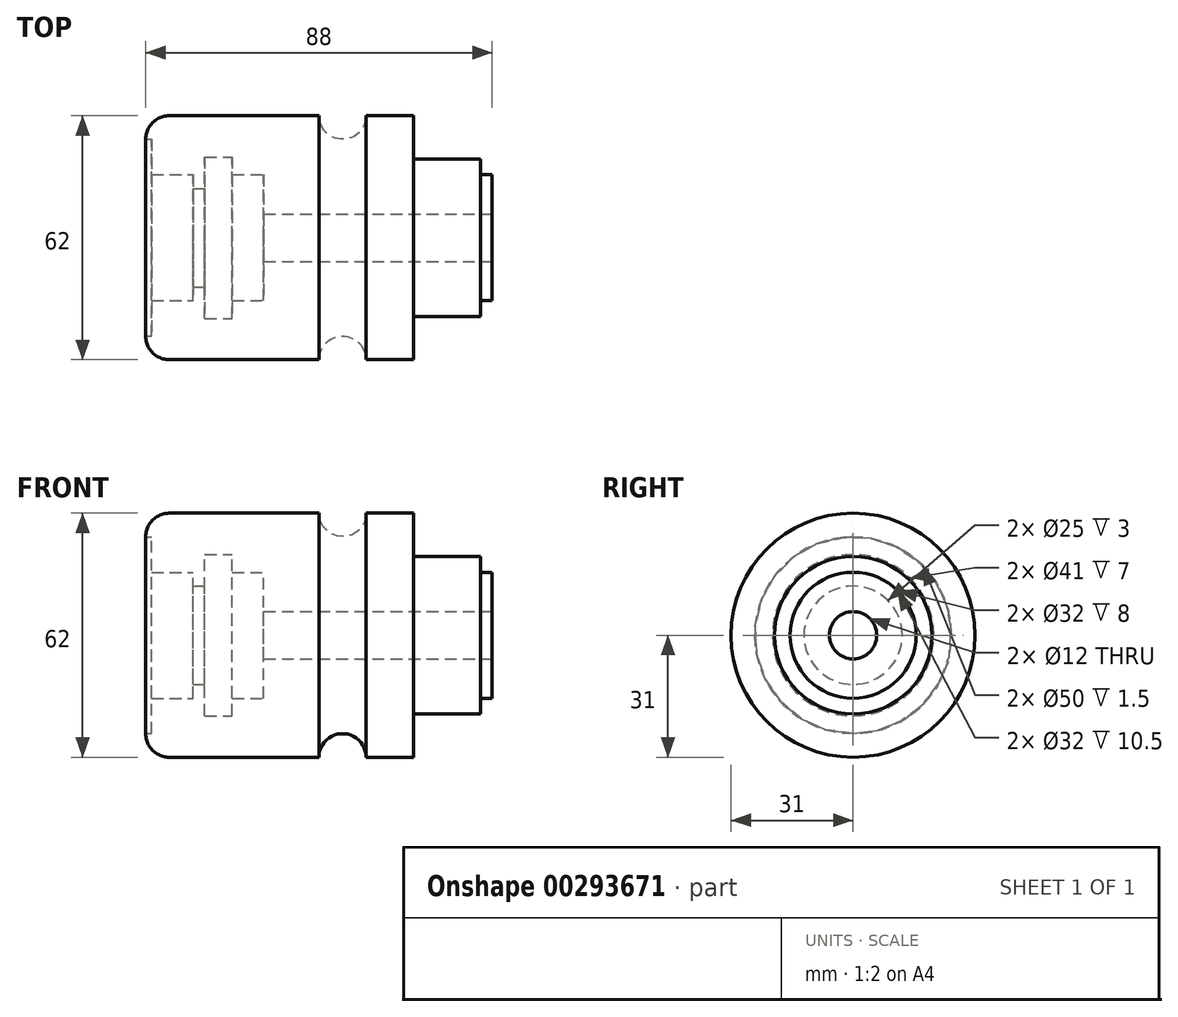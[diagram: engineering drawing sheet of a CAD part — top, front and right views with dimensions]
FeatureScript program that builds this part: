
annotation { "Feature Type Name" : "Feature", "Feature Type Description" : "" }
export const myFeature = defineFeature(function(context is Context, id is Id, definition is map)
    precondition{}
    {
        {
            var Q0;
            Q0=qCreatedBy(makeId("Front.planeOp"),FACE);
            var sketch = newSketch(context, id + "F0", { "sketchPlane" : qUnion([Q0])});
            skLineSegment(sketch, "E0", {"start": v(0, 31) * mm, "end": v(68, 31) * mm});
            skLineSegment(sketch, "E1", {"start": v(68, 31) * mm, "end": v(68, 20) * mm});
            skLineSegment(sketch, "E2", {"start": v(68, 20) * mm, "end": v(85, 20) * mm});
            skLineSegment(sketch, "E3", {"start": v(85, 20) * mm, "end": v(85, 16) * mm});
            skLineSegment(sketch, "E4", {"start": v(85, 16) * mm, "end": v(88, 16) * mm});
            skLineSegment(sketch, "E5", {"start": v(88, 16) * mm, "end": v(88, 0) * mm});
            skLineSegment(sketch, "E6", {"start": v(0, 0) * mm, "end": v(0, 31) * mm});
            skLineSegment(sketch, "E7", {"start": v(0, 25) * mm, "end": v(1.5, 25) * mm});
            skLineSegment(sketch, "E8", {"start": v(1.5, 25) * mm, "end": v(1.5, 0) * mm});
            skLineSegment(sketch, "E9", {"start": v(1.5, 16) * mm, "end": v(12, 16) * mm});
            skLineSegment(sketch, "E10", {"start": v(12, 16) * mm, "end": v(12, 0) * mm});
            skLineSegment(sketch, "E11", {"start": v(12, 12.5) * mm, "end": v(15, 12.5) * mm});
            skLineSegment(sketch, "E12", {"start": v(15, 0) * mm, "end": v(15, 20.5) * mm});
            skLineSegment(sketch, "E13", {"start": v(15, 20.5) * mm, "end": v(22, 20.5) * mm});
            skLineSegment(sketch, "E14", {"start": v(22, 20.5) * mm, "end": v(22, 0) * mm});
            skLineSegment(sketch, "E15", {"start": v(22, 16) * mm, "end": v(30, 16) * mm});
            skLineSegment(sketch, "E16", {"start": v(30, 16) * mm, "end": v(30, 0) * mm});
            skLineSegment(sketch, "E17", {"start": v(30, 6) * mm, "end": v(88, 6) * mm});
            skLineSegment(sketch, "E18.MirrorCS", {"start": v(0, 0) * mm, "end": v(0, -31) * mm});
            skLineSegment(sketch, "E19.MirrorCS", {"start": v(0, -31) * mm, "end": v(68, -31) * mm});
            skLineSegment(sketch, "E20.MirrorCS", {"start": v(68, -31) * mm, "end": v(68, -20) * mm});
            skLineSegment(sketch, "E21.MirrorCS", {"start": v(68, -20) * mm, "end": v(85, -20) * mm});
            skLineSegment(sketch, "E22.MirrorCS", {"start": v(85, -20) * mm, "end": v(85, -16) * mm});
            skLineSegment(sketch, "E23.MirrorCS", {"start": v(85, -16) * mm, "end": v(88, -16) * mm});
            skLineSegment(sketch, "E24.MirrorCS", {"start": v(30, -6) * mm, "end": v(88, -6) * mm});
            skLineSegment(sketch, "E25.MirrorCS", {"start": v(88, -16) * mm, "end": v(88, 0) * mm});
            skLineSegment(sketch, "E26.MirrorCS", {"start": v(30, -16) * mm, "end": v(30, 0) * mm});
            skLineSegment(sketch, "E27.MirrorCS", {"start": v(22, -20.5) * mm, "end": v(22, 0) * mm});
            skLineSegment(sketch, "E28.MirrorCS", {"start": v(15, -12.5) * mm, "end": v(15, 0) * mm});
            skLineSegment(sketch, "E29.MirrorCS", {"start": v(12, -16) * mm, "end": v(12, 0) * mm});
            skLineSegment(sketch, "E30.MirrorCS", {"start": v(1.5, -25) * mm, "end": v(1.5, 0) * mm});
            skLineSegment(sketch, "E31.MirrorCS", {"start": v(1.5, -16) * mm, "end": v(12, -16) * mm});
            skLineSegment(sketch, "E32.MirrorCS", {"start": v(12, -12.5) * mm, "end": v(15, -12.5) * mm});
            skLineSegment(sketch, "E33.MirrorCS", {"start": v(15, -20.5) * mm, "end": v(22, -20.5) * mm});
            skLineSegment(sketch, "E34.MirrorCS", {"start": v(22, -16) * mm, "end": v(30, -16) * mm});
            skLineSegment(sketch, "E35.MirrorCS", {"start": v(15, 0) * mm, "end": v(15, -20.5) * mm});
            skLineSegment(sketch, "E36.MirrorCS", {"start": v(0, -25) * mm, "end": v(1.5, -25) * mm});
            skCircle(sketch, "E37", {"center": v(50, 31) * mm, "radius": 6 * mm});
            skArc(sketch, "E38", {"start": v(6, 31) * mm, "mid": v(1.76, 29.24) * mm, "end": v(0, 25) * mm});
            skArc(sketch, "E39.MirrorCS", {"start": v(6, -31) * mm, "mid": v(1.76, -29.24) * mm, "end": v(0, -25) * mm});
            skCircle(sketch, "E40.MirrorC", {"center": v(50, -31) * mm, "radius": 6 * mm});
            skLineSegment(sketch, "E41", {"start": v(88, 0) * mm, "end": v(0, 0) * mm, "construction": true});
            skSolve(sketch);
        }
        {
            var Q0;
            {var subQ11=sQuery(id+"F0.wireOp",EDGE,"E1");Q0=makeQuery(id+"F0.imprint","IMPRINT",FACE,{"disambiguationData":[TD([[makeQuery(id+"F0.imprint","IMPRINT",EDGE,{"derivedFrom":subQ11}),-1.0]])]});}
            var Q1;
            {var subQ14=sQuery(id+"F0.wireOp",EDGE,"E20.MirrorCS");Q1=makeQuery(id+"F0.imprint","IMPRINT",FACE,{"disambiguationData":[TD([[makeQuery(id+"F0.imprint","IMPRINT",EDGE,{"derivedFrom":subQ14}),1.0]])]});}
            var Q2;
            Q2=sQuery(id+"F0.wireOp",EDGE,"E41");
            revolve(context, id + "F1", {"entities" : qUnion([Q0, Q1]), "axis" : qUnion([Q2]), "revolveType" : RevolveType.FULL});
        }
    });
